# Revit family: Ginko 3.0
name_source: partatom
category: Lighting Fixtures
revit_build: Autodesk Revit 2017 (Build: 20160225_1515(x64)
units: mm (PartAtom-declared; Revit-internal decimal feet)

## family parameters
Always vertical = No
Cut with Voids When Loaded = No
Light Source = No
OmniClass Number = 23.80.70.00
OmniClass Title = Lighting
Part Type = Normal
Room Calculation Point = No
Round Connector Dimension = Use Diameter
Shared = No
Work Plane-Based = Yes

## types (8) — shared parameters
Apparent Load Phase 1 = 15 W
Base = L&L_White
Base bracket = Ginko3.0_Base bracket
Bracket = L&L_Stainless steel
CRI = 90 (also available: CRI 80 - ref. URL Technical sheet)
Code = GN300 I Stainless steel; GN300 E White; GN300 N Black anodized; GN300 F Grey; GN300 H Anthracite; GN300 T Cor-ten; GN300 5 Jasper green
Control system = -
Cutout dimensions = -
Default Elevation = 1219 mm
Delivered lumen output = 750 lm (3000K, 42°, 10W, CRI 80); 609 lm (3000K, 42°, 10W, CRI 90); 1162 lm (3000K, 42°, 15W, CRI 80); 945 lm (3000K, 42°, 15W, CRI 90)
Description = Outdoor projectors
Energy efficiency class = A A+ A++
Features = 12°x64°, 28°x72° optics and shadow-effect filter, adjustable through 360° using the magnet provided
Geometry = Ginko3.0_mod : Ginko_3.0
H1 = 75 mm
Height mm = 158 mm
IP = 66
Length mm = 88 mm  [stored 0.288714 ft]
Lens = L&L_Lens
Lumen output at source = 1096 lm (3000K, 10W, CRI 80); 886 lm (3000K, 10W, CRI 90); 1662 lm (3000K, 15W, CRI 80); 1343 lm (3000K, 15W, CRI 90)
Manufacturer = L&L Luce&Light
Material = body in AISI 316L stainless steel or anticorodal aluminium, AISI 316L stainless steel bracket, screen in tempered, transparent extra-clear glass
Middle = L&L_White
Model = Ginko 3.0
Mounting = surface mounted (ceiling, wall, ground, spike)
No. and type of led = 1 high power density COB LED; 2-step MacAdam; 50000h L95 B10 (Ta 25°C)
Notes = -
Power = 15W (also available: 10W - ref. URL Technical sheet)
Power cables = includes 1,5 m neoprene cable, H05RN-F 2x0,75/0,75 Ø6,3 mm
Power supply = 24Vdc
Power supply unit = not included
Top = L&L_White
URL = https://www.lucelight.it
URL Accessories and power supply units = https://www.lucelight.it
URL Catalogue = https://www.lucelight.it
URL DXF = https://www.lucelight.it
URL Description = https://www.lucelight.it
URL General code = https://www.lucelight.it
URL IES Photometric file = https://www.lucelight.it
URL Image = https://www.lucelight.it
URL Technical sheet = https://www.lucelight.it
Vertical rotation max = 190.00°
Voltage = 24 V
Weight kg = 1.04
Width mm = 84 mm  [stored 0.275591 ft]
Wiring = -
X1 = 100 mm  [stored 0.328084 ft]

## per-type parameters (varying)
| type | LED Colour | Light Source | Optics |
| Ginko 3.0_J 58° (3000K 15W 24Vdc) | 3000K (also available: 2700K and 4000K - ref. URL Technical sheet) | Light Source_3.0 : J58° | 58° |
| Ginko 3.0_L 42° (3000K 15W 24Vdc) | 3000K (also available: 2700K and 4000K - ref. URL Technical sheet) | Light Source_3.0 : L42° | 42° |
| Ginko 3.0_M 30° (3000K 15W 24Vdc) | 3000K (also available: 2700K and 4000K - ref. URL Technical sheet) | Light Source_3.0 : M30° | 30° |
| Ginko 3.0_P 48° (3000K 15W 24Vdc) | 3000K (also available: 2700K and 4000K - ref. URL Technical sheet) | Light Source_3.0 : P48° | 48° |
| Ginko 3.0_P+WR8000 (3000K 15W 24Vdc) | 3000K (also available: 2700K and 4000K - ref. URL Technical sheet) | Light Source_3.0 : P+WR8000° | WR8000 |
| Ginko 3.0_S 13° (3000K 15W 24Vdc) | 3000K (also available: 2700K and 4000K - ref. URL Technical sheet) | Light Source_3.0 : S13° | 13° |
| Ginko 3.0_W 12°x64° magnet (3000K 15W 24Vdc) | 3000K (also available: 2700K and 4000K - ref. URL Technical sheet) | Light Source_3.0 : W12°x64° | 12°x64° |
| Ginko 3.0_X 28°x72° magnet (3000K 15W 24Vdc) | 3000K (also available: 2700K and 4000K - ref. URL Technical sheet) | Light Source_3.0 : X28°x72° | 28°x72° |

note: [stored X ft] marks values corroborated as IEEE doubles in the binary element streams (Revit-internal decimal feet)

## geometry (parser evidence)
native form markers: Blend x2, Sweep x7
no freeform markers — native parametric forms only
